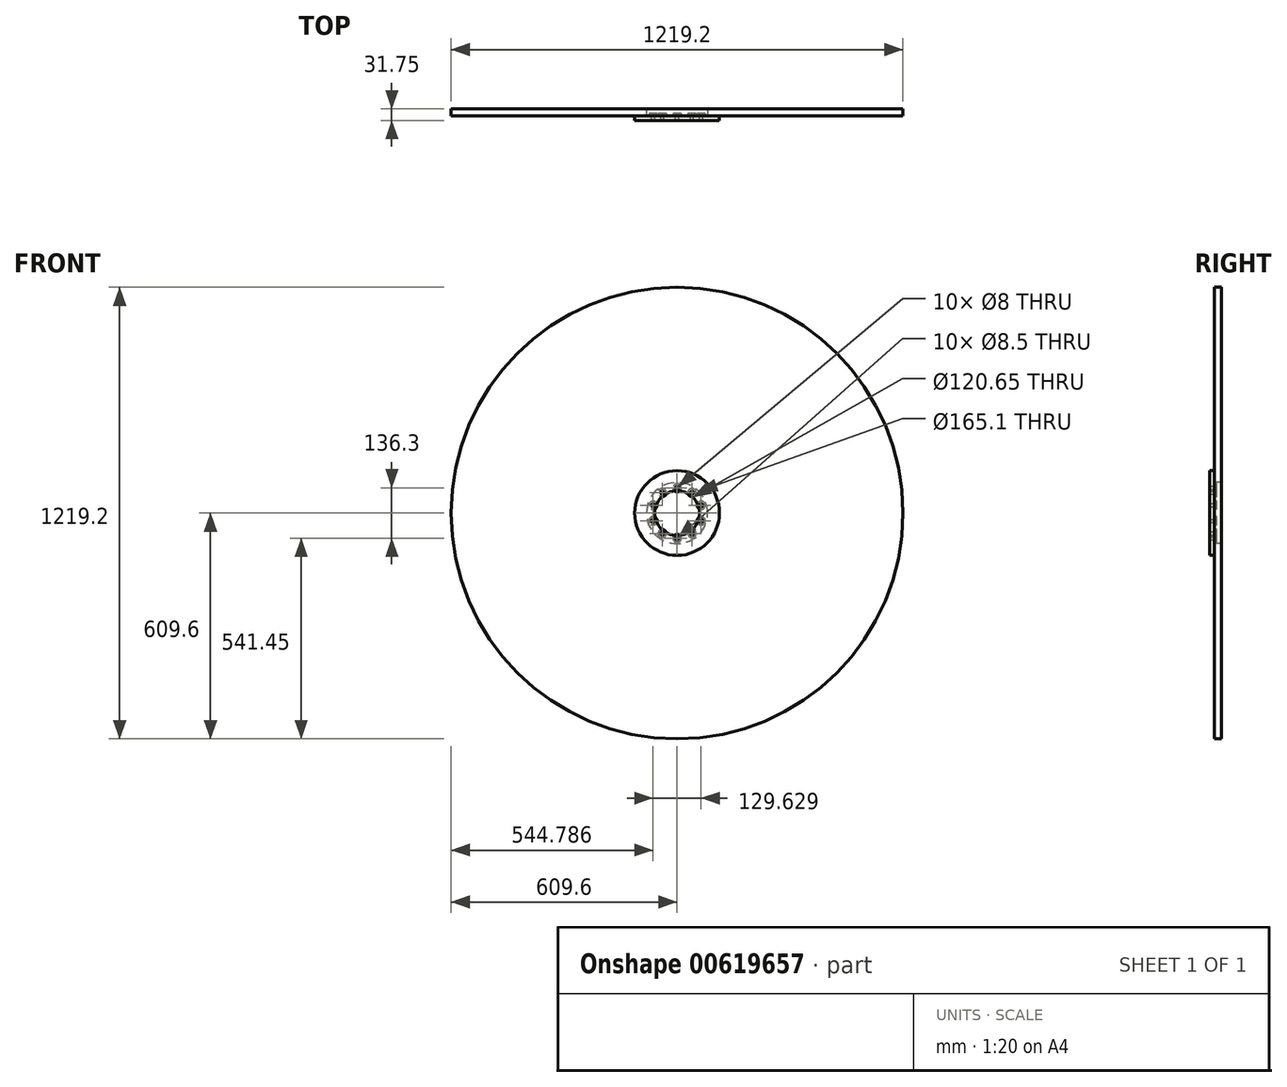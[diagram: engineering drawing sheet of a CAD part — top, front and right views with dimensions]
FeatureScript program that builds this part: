
annotation { "Feature Type Name" : "Feature", "Feature Type Description" : "" }
export const myFeature = defineFeature(function(context is Context, id is Id, definition is map)
    precondition{}
    {
        {
            var Q0;
            Q0=qCreatedBy(makeId("Front.planeOp"),FACE);
            var sketch = newSketch(context, id + "F0", { "sketchPlane" : qUnion([Q0])});
            skCircle(sketch, "E0", {"center": v(0, 0) * mm, "radius": 57.15 * mm, "construction": true});
            skCircle(sketch, "E1", {"center": v(0, 68.15) * mm, "radius": 11 * mm});
            skCircle(sketch, "E2", {"center": v(0, 68.15) * mm, "radius": 4 * mm});
            skCircle(sketch, "E3.0", {"center": v(0, 0) * mm, "radius": 68.15 * mm, "construction": true});
            skCircle(sketch, "E4.1.0", {"center": v(-40.06, 55.13) * mm, "radius": 4 * mm});
            skCircle(sketch, "E4.1.1", {"center": v(-40.06, 55.13) * mm, "radius": 11 * mm});
            skCircle(sketch, "E4.2.0", {"center": v(-64.81, 21.06) * mm, "radius": 4 * mm});
            skCircle(sketch, "E4.2.1", {"center": v(-64.81, 21.06) * mm, "radius": 11 * mm});
            skCircle(sketch, "E4.3.0", {"center": v(-64.81, -21.06) * mm, "radius": 4 * mm});
            skCircle(sketch, "E4.3.1", {"center": v(-64.81, -21.06) * mm, "radius": 11 * mm});
            skCircle(sketch, "E4.4.0", {"center": v(-40.06, -55.13) * mm, "radius": 4 * mm});
            skCircle(sketch, "E4.4.1", {"center": v(-40.06, -55.13) * mm, "radius": 11 * mm});
            skCircle(sketch, "E4.5.0", {"center": v(0, -68.15) * mm, "radius": 4 * mm});
            skCircle(sketch, "E4.5.1", {"center": v(0, -68.15) * mm, "radius": 11 * mm});
            skCircle(sketch, "E4.6.0", {"center": v(40.06, -55.13) * mm, "radius": 4 * mm});
            skCircle(sketch, "E4.6.1", {"center": v(40.06, -55.13) * mm, "radius": 11 * mm});
            skCircle(sketch, "E4.7.0", {"center": v(64.81, -21.06) * mm, "radius": 4 * mm});
            skCircle(sketch, "E4.7.1", {"center": v(64.81, -21.06) * mm, "radius": 11 * mm});
            skCircle(sketch, "E4.8.0", {"center": v(64.81, 21.06) * mm, "radius": 4 * mm});
            skCircle(sketch, "E4.8.1", {"center": v(64.81, 21.06) * mm, "radius": 11 * mm});
            skCircle(sketch, "E4.9.0", {"center": v(40.06, 55.13) * mm, "radius": 4 * mm});
            skCircle(sketch, "E4.9.1", {"center": v(40.06, 55.13) * mm, "radius": 11 * mm});
            skSolve(sketch);
        }
        {
            var Q0;
            Q0 = qSketchRegion(id + "F0", true);
            extrude(context, id + "F1", {"entities" : qUnion([Q0]), "endBound" : BoundingType.SYMMETRIC, "oppositeDirection" : true, "depth" : 7 * mm, "offsetDistance" : 25.4 * mm});
        }
        {
            var Q0;
            Q0=makeQuery(id+"F1.opExtrude","CAP_FACE",FACE,{"disambiguationData":[OSD([sQuery(id+"F0.wireOp",EDGE,"E1"),sQuery(id+"F0.wireOp",EDGE,"E2")])],"isStart":true});
            var sketch = newSketch(context, id + "F2", { "sketchPlane" : qUnion([Q0])});
            skCircle(sketch, "E5", {"center": v(0, 0) * mm, "radius": 60.33 * mm});
            skCircle(sketch, "E6", {"center": v(0, 0) * mm, "radius": 114.3 * mm});
            skCircle(sketch, "E7", {"center": v(0, 0) * mm, "radius": 82.55 * mm});
            skCircle(sketch, "E8", {"center": v(0, 0) * mm, "radius": 609.6 * mm});
            skCircle(sketch, "E9", {"center": v(0, 68.15) * mm, "radius": 4.25 * mm});
            skCircle(sketch, "E10.1.0", {"center": v(-40.06, 55.13) * mm, "radius": 4.25 * mm});
            skCircle(sketch, "E10.2.0", {"center": v(-64.81, 21.06) * mm, "radius": 4.25 * mm});
            skCircle(sketch, "E10.3.0", {"center": v(-64.81, -21.06) * mm, "radius": 4.25 * mm});
            skCircle(sketch, "E10.4.0", {"center": v(-40.06, -55.13) * mm, "radius": 4.25 * mm});
            skCircle(sketch, "E10.5.0", {"center": v(0, -68.15) * mm, "radius": 4.25 * mm});
            skCircle(sketch, "E10.6.0", {"center": v(40.06, -55.13) * mm, "radius": 4.25 * mm});
            skCircle(sketch, "E10.7.0", {"center": v(64.81, -21.06) * mm, "radius": 4.25 * mm});
            skCircle(sketch, "E10.8.0", {"center": v(64.81, 21.06) * mm, "radius": 4.25 * mm});
            skCircle(sketch, "E10.9.0", {"center": v(40.06, 55.13) * mm, "radius": 4.25 * mm});
            skSolve(sketch);
        }
        {
            var Q0;
            Q0=makeQuery(id+"F2.imprint","IMPRINT",FACE,{"disambiguationData":[TD([[makeQuery(id+"F2.imprint","IMPRINT",EDGE,{"derivedFrom":sQuery(id+"F2.wireOp",EDGE,"E7")}),1.0]])]});
            var Q1;
            Q1=makeQuery(id+"F2.imprint","IMPRINT",FACE,{"disambiguationData":[TD([[makeQuery(id+"F2.imprint","IMPRINT",EDGE,{"derivedFrom":sQuery(id+"F2.wireOp",EDGE,"E6")}),1.0]])]});
            var Q2;
            Q2=makeQuery(id+"F2.imprint","IMPRINT",FACE,{"disambiguationData":[TD([[makeQuery(id+"F2.imprint","IMPRINT",EDGE,{"derivedFrom":sQuery(id+"F2.wireOp",EDGE,"E9")}),-1.0]])]});
            extrude(context, id + "F3", {"entities" : qUnion([Q0, Q1, Q2]), "depth" : 12.7 * mm, "offsetDistance" : 25.4 * mm});
        }
        {
            var Q0;
            Q0=makeQuery(id+"F2.imprint","IMPRINT",FACE,{"disambiguationData":[TD([[makeQuery(id+"F2.imprint","IMPRINT",EDGE,{"derivedFrom":sQuery(id+"F2.wireOp",EDGE,"E6")}),-1.0]])]});
            var Q1;
            Q1=makeQuery(id+"F2.imprint","IMPRINT",FACE,{"disambiguationData":[TD([[makeQuery(id+"F2.imprint","IMPRINT",EDGE,{"derivedFrom":sQuery(id+"F2.wireOp",EDGE,"E6")}),1.0]])]});
            extrude(context, id + "F4", {"entities" : qUnion([Q0, Q1]), "oppositeDirection" : true, "depth" : 19.05 * mm, "offsetDistance" : 25.4 * mm});
        }
    });
